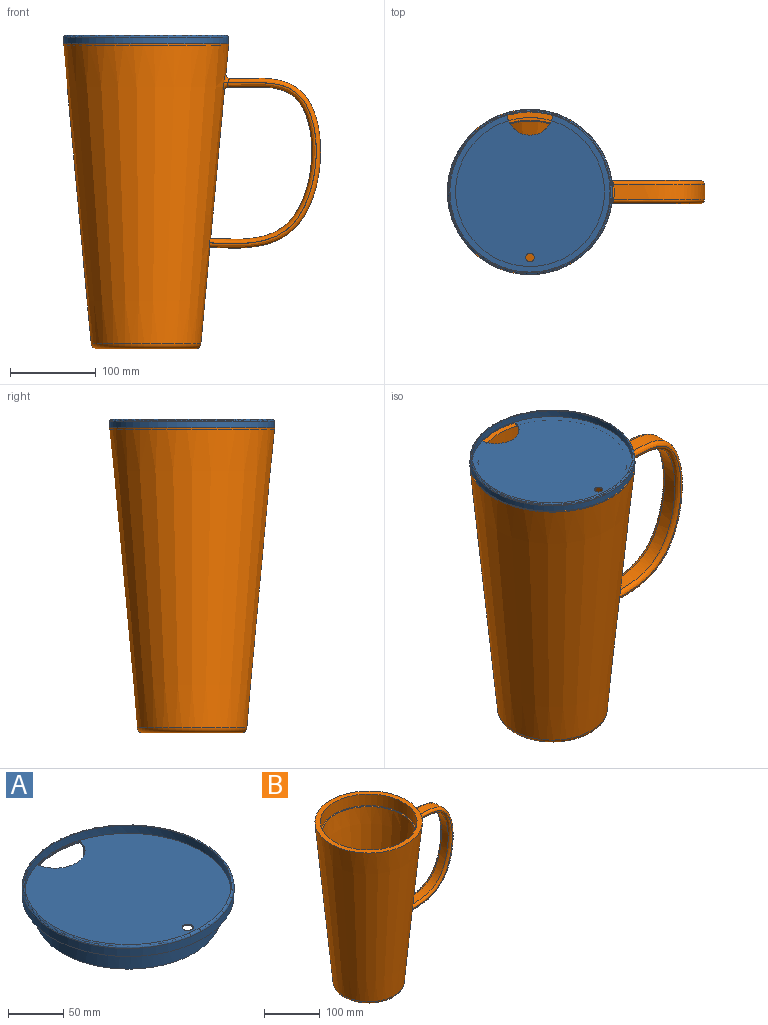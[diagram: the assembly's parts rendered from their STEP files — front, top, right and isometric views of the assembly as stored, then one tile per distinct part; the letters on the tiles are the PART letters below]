
ASSEMBLY  parts=2 mates=1
PART A: 22 faces, bbox 207.8x207.8x34.3 mm
  f0: plane 186.94x182.99mm, normal (0,0,1), area 26281.5mm2, adj f10,f20,f21
  f1: plane 27.64x4.69mm, normal (0,0,1), area 3.7mm2, adj f10,f19
  f2: plane 27.64x4.69mm, normal (0,0,1), area 3.7mm2, adj f10,f19
  f3: plane 192.02x192.02mm, normal (0,0,-1), area 6332.4mm2, adj f4,f9,f16,f17,f18
  f4: cylinder r=83.95mm len=167.89mm, axis (0,0,1), area 10788.3mm2, adj f3,f8,f16,f17
  f5: plane 189.99x189.99mm, normal (0,0,1), area 6206.7mm2, adj f7,f12,f16,f17,f18
  f6: plane 188.98x188.98mm, normal (0,0,-1), area 26888.9mm2, adj f13,f19,f20,f21
  f7: cylinder r=82.93mm len=165.86mm, axis (0,0,1), area 11316mm2, adj f5,f8,f15,f16,f17
  f8: cone r=76.33mm half-angle=71deg, axis (0,0,1), area 513.6mm2, adj f4,f7,f15,f16,f17
  f9: cylinder r=96.01mm len=192.02mm, axis (0,0,-1), area 5363mm2, adj f3,f11
  f10: cylinder r=93.47mm len=186.94mm, axis (0,0,-1), area 5221.1mm2, adj f0,f1,f2,f11
  f11: torus R=93.47mm, axis (0,0,1), area 2383.8mm2, adj f9,f10
  f12: cylinder r=95mm len=189.99mm, axis (0,0,-1), area 4699.8mm2, adj f5,f14
  f13: cylinder r=94.49mm len=188.98mm, axis (0,0,-1), area 5047.5mm2, adj f6,f14
  f14: torus R=93.47mm, axis (0,0,1), area 763.7mm2, adj f12,f13
  f15: plane 46.78x3.4mm, normal (0,0,1), area 1.7mm2, adj f7,f8,f16,f17
  f16: cylinder r=27.19mm len=23.88mm, axis (0,0,1), area 34.5mm2, adj f3,f4,f5,f7,f8,f15,f18
  f17: cylinder r=27.19mm len=23.88mm, axis (0,0,1), area 34.5mm2, adj f3,f4,f5,f7,f8,f15,f18
  f18: extruded ~53.81x3.96mm, area 55.4mm2, adj f3,f5,f16,f17
  f19: extruded ~53.81x3.96mm, area 55.4mm2, adj f1,f2,f6,f20
  f20: cylinder r=27.19mm len=53.81mm, axis (0,0,1), area 78.7mm2, adj f0,f6,f19
  f21: cylinder r=4.94mm len=9.89mm, axis (0,0,1), area 31.6mm2, adj f0,f6
PART B: 30 faces, bbox 300.7x193x428.7 mm
  f0: cone r=53.92mm half-angle=5.3deg, axis (0,0,1), area 97847.9mm2, adj f1,f2,f3,f4,f9
  f1: plane 8.55x0.81mm, normal (0,-1,0), area 3.4mm2, adj f0,f2,f4
  f2: bspline ~78.3x27.05mm, area 15mm2, adj f0,f1,f3,f4
  f3: plane 8.55x0.81mm, normal (0,1,0), area 3.4mm2, adj f0,f2,f4
  f4: cylinder r=64.52mm len=129.03mm, axis (0,0,-1), area 3207.3mm2, adj f0,f1,f2,f3,f5
  f5: plane 129.03x129.03mm, normal (0,0,1), area 274.7mm2, adj f4,f7
  f6: plane 108.48x108.48mm, normal (0,0,1), area 9242.4mm2, adj f7
  f7: cone r=53.92mm half-angle=5.3deg, axis (0,0,1), area 38496.5mm2, adj f5,f6
  f8: cylinder r=86.88mm len=173.77mm, axis (0,0,1), area 13865.8mm2, adj f9,f29
  f9: plane 173.77x173.77mm, normal (0,0,1), area 1569.7mm2, adj f0,f8
  f10: plane 115.42x115.42mm, normal (0,0,-1), area 10463.7mm2, adj f11
  f11: torus R=57.71mm, axis (0,0,1), area 3633.7mm2, adj f10,f28
  f12: bspline ~198.41x136.79mm, area 2871.7mm2, adj f13,f19,f21,f28
  f13: bspline ~198.59x170.42mm, area 6152.3mm2, adj f12,f14,f20,f28
  f14: bspline ~198.41x136.79mm, area 2871.6mm2, adj f13,f15,f27,f28
  f15: plane 188.25x124.96mm, normal (0,1,0), area 28.5mm2, adj f14,f16,f26,f28
  f16: bspline ~188.09x132.42mm, area 2710.3mm2, adj f15,f17,f25,f28
  f17: bspline ~178.11x159.42mm, area 5620.4mm2, adj f16,f18,f24,f28
  f18: bspline ~188.09x132.42mm, area 2710.3mm2, adj f17,f19,f23,f28
  f19: plane 188.25x124.96mm, normal (0,-1,0), area 28.5mm2, adj f12,f18,f22,f28
  f20: bspline ~21.21x6mm, area 136.1mm2, adj f13,f21,f27,f28
  f21: bspline ~12.31x11.32mm, area 82.9mm2, adj f12,f20,f22,f28
  f22: bspline ~237.12x27.33mm, area 0.5mm2, adj f19,f21,f23,f28
  f23: bspline ~11.92x11.8mm, area 79.3mm2, adj f18,f22,f24,f28
  f24: bspline ~22.84x5.95mm, area 126mm2, adj f17,f23,f25,f28
  f25: bspline ~12.43x11.15mm, area 79.3mm2, adj f16,f24,f26,f28
  f26: bspline ~237.12x27.33mm, area 0.5mm2, adj f15,f25,f27,f28
  f27: bspline ~11.92x11.76mm, area 82.9mm2, adj f14,f20,f26,f28
  f28: cone r=64.04mm half-angle=5.3deg, axis (0,0,1), area 176320.5mm2, adj f11,f12,f13,f14,f15,f16,f17,f18
  f29: plane 193.04x193.04mm, normal (0,0,1), area 5552.9mm2, adj f8,f28
PLACE A t=(-48.86,-31.81,238.39)mm
PLACE B t=(-48.86,-31.81,-2.19)mm
MATE fastened A.f9 <-> B.f0  axis (0,0,-1) through (-48.86,-31.81,239.92)mm
